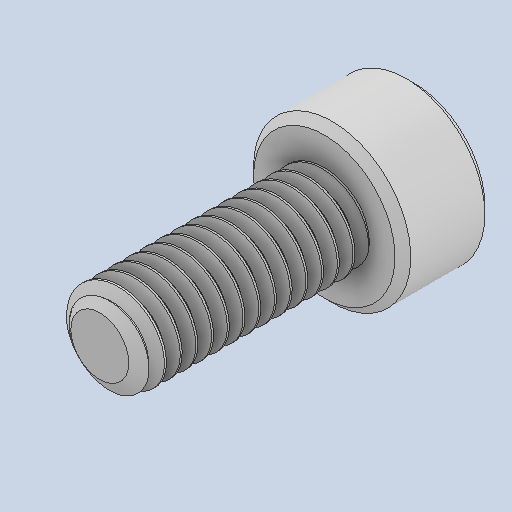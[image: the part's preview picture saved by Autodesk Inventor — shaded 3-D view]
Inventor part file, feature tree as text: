
AUTODESK INVENTOR PART (.ipt)
format: ipt  version: 2023 (Build 270158000, 158)  size: 548,352 bytes
history: native  units: in
note: dims shown in document units (in); Inventor stores cm internally (conversion verified against a paired STEP export)
features: chamfer x1
ambient origin geometry x8: Origin, YZ Plane, XZ Plane, XY Plane, X Axis, Y Axis, Z Axis, Center Point
bodies: Solid1 (feature_tree)
feature tree (1):
  chamfer  "Chamfer1"  [1 undecoded]
note: 1 required parameter value undecoded (feature->parameter linkage not recoverable at this tier; creation-order binding heuristic only, values carry confidence <= 0.55)
